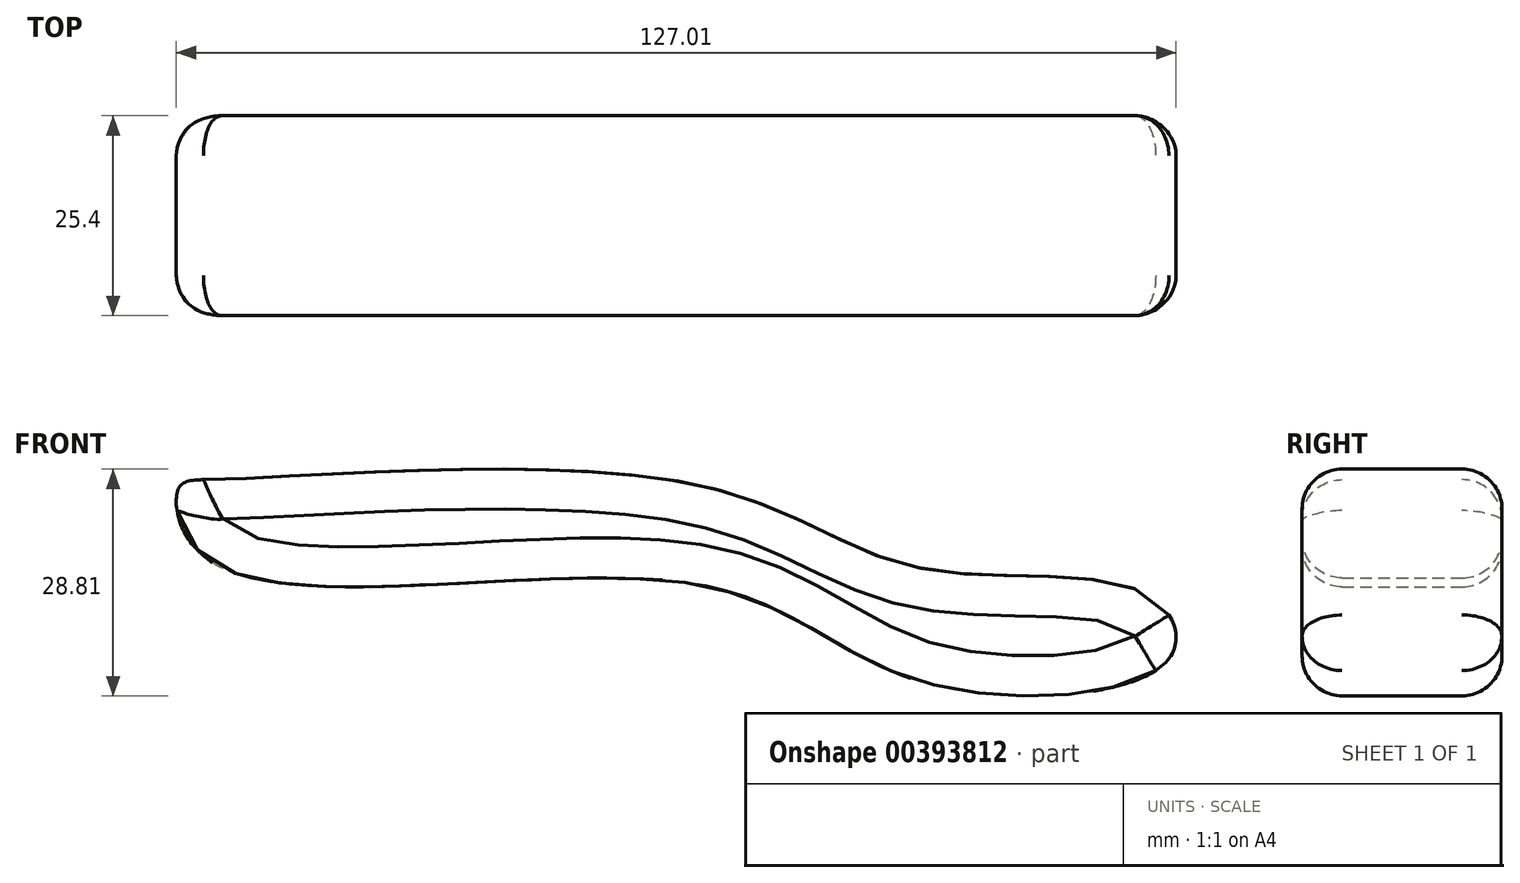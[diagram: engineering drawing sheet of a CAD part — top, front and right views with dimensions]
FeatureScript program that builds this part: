
annotation { "Feature Type Name" : "Feature", "Feature Type Description" : "" }
export const myFeature = defineFeature(function(context is Context, id is Id, definition is map)
    precondition{}
    {
        {
            var Q0;
            Q0=qCreatedBy(makeId("Front.planeOp"),FACE);
            var sketch = newSketch(context, id + "F0", { "sketchPlane" : qUnion([Q0])});
            skFitSpline(sketch, "E0", {"points": [v(-60.45, 30.45) * mm, v(0, 29.78) * mm, v(28.67, 19.11) * mm, v(57.34, 15.78) * mm, v(60, 7.56) * mm, v(28.9, 4.67) * mm, v(0, 17.11) * mm, v(-60.9, 19.56) * mm, v(-65.79, 29.11) * mm, v(-60.45, 30.45) * mm]});
            skSolve(sketch);
        }
        {
            var Q0;
            Q0=makeQuery(id+"F0.imprint","IMPRINT",FACE,{"disambiguationData":[TD([[makeQuery(id+"F0.imprint","IMPRINT",EDGE,{"derivedFrom":sQuery(id+"F0.wireOp",EDGE,"E0")}),-1.0]])]});
            extrude(context, id + "F1", {"entities" : qUnion([Q0]), "depth" : 25.4 * mm});
        }
        {
            var Q0;
            Q0=makeQuery(id+"F1.opExtrude","CAP_EDGE",EDGE,{"disambiguationData":[OSD([sQuery(id+"F0.wireOp",EDGE,"E0")])],"isStart":false});
            var Q1;
            Q1=makeQuery(id+"F1.opExtrude","CAP_EDGE",EDGE,{"disambiguationData":[OSD([sQuery(id+"F0.wireOp",EDGE,"E0")])],"isStart":true});
            fillet(context, id + "F2", {"entities" : qUnion([Q0, Q1]), "radius" : 5.08 * mm, "tangentPropagation" : true, "allowEdgeOverflow" : false});
        }
        {
            var Q0;
            Q0=qCreatedBy(makeId("Right.planeOp"),FACE);
            var sketch = newSketch(context, id + "F3", { "sketchPlane" : qUnion([Q0])});
            skCircle(sketch, "E1", {"center": v(47.66, -71.83) * mm, "radius": 6.18 * mm});
            skSolve(sketch);
        }
        {
            var Q0;
            Q0 = qSketchRegion(id + "F3", true);
            extrude(context, id + "F4", {"entities" : qUnion([Q0]), "operationType" : NewBodyOperationType.REMOVE, "oppositeDirection" : true, "depth" : 25.4 * mm});
        }
    });
